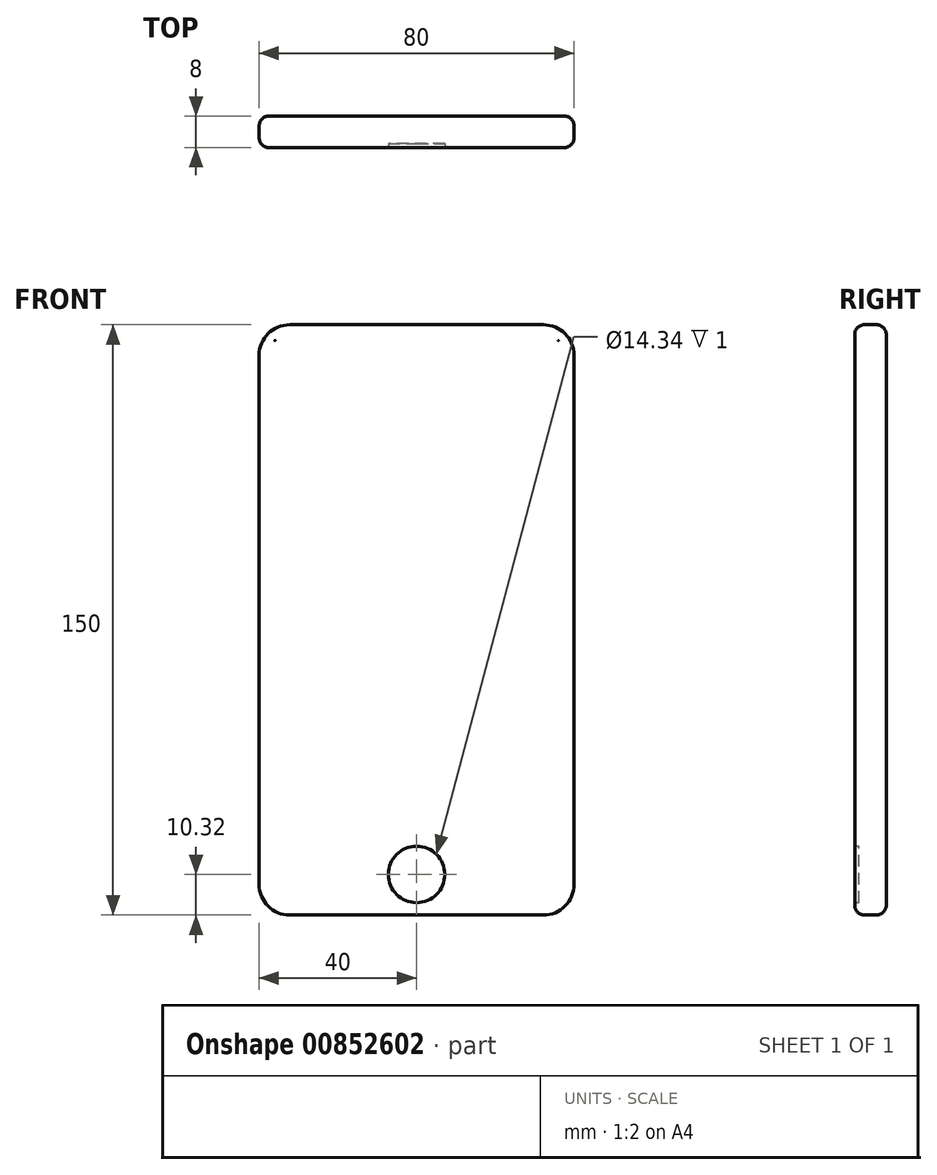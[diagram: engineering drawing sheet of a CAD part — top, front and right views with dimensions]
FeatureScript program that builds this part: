
annotation { "Feature Type Name" : "Feature", "Feature Type Description" : "" }
export const myFeature = defineFeature(function(context is Context, id is Id, definition is map)
    precondition{}
    {
        {
            var Q0;
            Q0=qCreatedBy(makeId("Front.planeOp"),FACE);
            var sketch = newSketch(context, id + "F0", { "sketchPlane" : qUnion([Q0])});
            skLineSegment(sketch, "E0.bottom", {"start": v(32.2, 75) * mm, "end": v(-32.2, 75) * mm});
            skLineSegment(sketch, "E0.top", {"start": v(32.2, -75) * mm, "end": v(-32.2, -75) * mm});
            skLineSegment(sketch, "E0.left", {"start": v(40, 67.2) * mm, "end": v(40, -67.2) * mm});
            skLineSegment(sketch, "E0.right", {"start": v(-40, 67.2) * mm, "end": v(-40, -67.2) * mm});
            skPoint(sketch, "E0.middle", {"position": v(0, 0) * mm});
            skLineSegment(sketch, "E1.0", {"start": v(36, 71) * mm, "end": v(-36, 71) * mm});
            skLineSegment(sketch, "E1.1", {"start": v(36, 71) * mm, "end": v(36, -54.77) * mm});
            skLineSegment(sketch, "E1.3", {"start": v(-36, 71) * mm, "end": v(-36, -54.77) * mm});
            skLineSegment(sketch, "E2", {"start": v(-36, -54.77) * mm, "end": v(36, -54.77) * mm});
            skCircle(sketch, "E3", {"center": v(0, -64.68) * mm, "radius": 7.17 * mm});
            skPoint(sketch, "E4.visualSharp", {"position": v(-40, 75) * mm});
            skArc(sketch, "E4.filletArc", {"start": v(-32.2, 75) * mm, "mid": v(-37.72, 72.72) * mm, "end": v(-40, 67.2) * mm});
            skPoint(sketch, "E5.visualSharp", {"position": v(40, 75) * mm});
            skArc(sketch, "E5.filletArc", {"start": v(40, 67.2) * mm, "mid": v(37.72, 72.72) * mm, "end": v(32.2, 75) * mm});
            skPoint(sketch, "E6.visualSharp", {"position": v(40, -75) * mm});
            skArc(sketch, "E6.filletArc", {"start": v(32.2, -75) * mm, "mid": v(37.72, -72.72) * mm, "end": v(40, -67.2) * mm});
            skPoint(sketch, "E7.visualSharp", {"position": v(-40, -75) * mm});
            skArc(sketch, "E7.filletArc", {"start": v(-40, -67.2) * mm, "mid": v(-37.72, -72.72) * mm, "end": v(-32.2, -75) * mm});
            skSolve(sketch);
        }
        {
            var Q0;
            Q0=makeQuery(id+"F0.imprint","IMPRINT",FACE,{"disambiguationData":[TD([[makeQuery(id+"F0.imprint","IMPRINT",EDGE,{"derivedFrom":sQuery(id+"F0.wireOp",EDGE,"E0.bottom")}),1.0]])]});
            var Q1;
            Q1=makeQuery(id+"F0.imprint","IMPRINT",FACE,{"disambiguationData":[TD([[makeQuery(id+"F0.imprint","IMPRINT",EDGE,{"derivedFrom":sQuery(id+"F0.wireOp",EDGE,"E3")}),1.0]])]});
            extrude(context, id + "F1", {"entities" : qUnion([Q0, Q1]), "oppositeDirection" : true, "depth" : 8 * mm, "offsetDistance" : 25 * mm});
        }
        {
            var Q0;
            Q0=makeQuery(id+"F1.opExtrude","CAP_EDGE",EDGE,{"disambiguationData":[OSD([sQuery(id+"F0.wireOp",EDGE,"E0.bottom")])],"isStart":false});
            fillet(context, id + "F2", {"entities" : qUnion([Q0]), "radius" : 2.5 * mm, "tangentPropagation" : true, "allowEdgeOverflow" : false});
        }
        {
            var Q0;
            Q0=makeQuery(id+"F1.opExtrude","CAP_EDGE",EDGE,{"disambiguationData":[OSD([sQuery(id+"F0.wireOp",EDGE,"E0.bottom")])],"isStart":true});
            fillet(context, id + "F3", {"entities" : qUnion([Q0]), "radius" : 2.5 * mm, "tangentPropagation" : true, "allowEdgeOverflow" : false});
        }
        {
            var Q0;
            Q0=makeQuery(id+"F0.imprint","IMPRINT",FACE,{"disambiguationData":[TD([[makeQuery(id+"F0.imprint","IMPRINT",EDGE,{"derivedFrom":sQuery(id+"F0.wireOp",EDGE,"E3")}),1.0]])]});
            extrude(context, id + "F4", {"entities" : qUnion([Q0]), "operationType" : NewBodyOperationType.REMOVE, "oppositeDirection" : true, "depth" : 1 * mm, "offsetDistance" : 25 * mm});
        }
        {
            var Q0;
            Q0=makeQuery(id+"F0.imprint","IMPRINT",FACE,{"disambiguationData":[TD([[makeQuery(id+"F0.imprint","IMPRINT",EDGE,{"derivedFrom":sQuery(id+"F0.wireOp",EDGE,"E1.0")}),1.0]])]});
            extrude(context, id + "F5", {"entities" : qUnion([Q0]), "operationType" : NewBodyOperationType.ADD, "oppositeDirection" : true, "depth" : 8 * mm, "offsetDistance" : 25 * mm});
        }
    });
